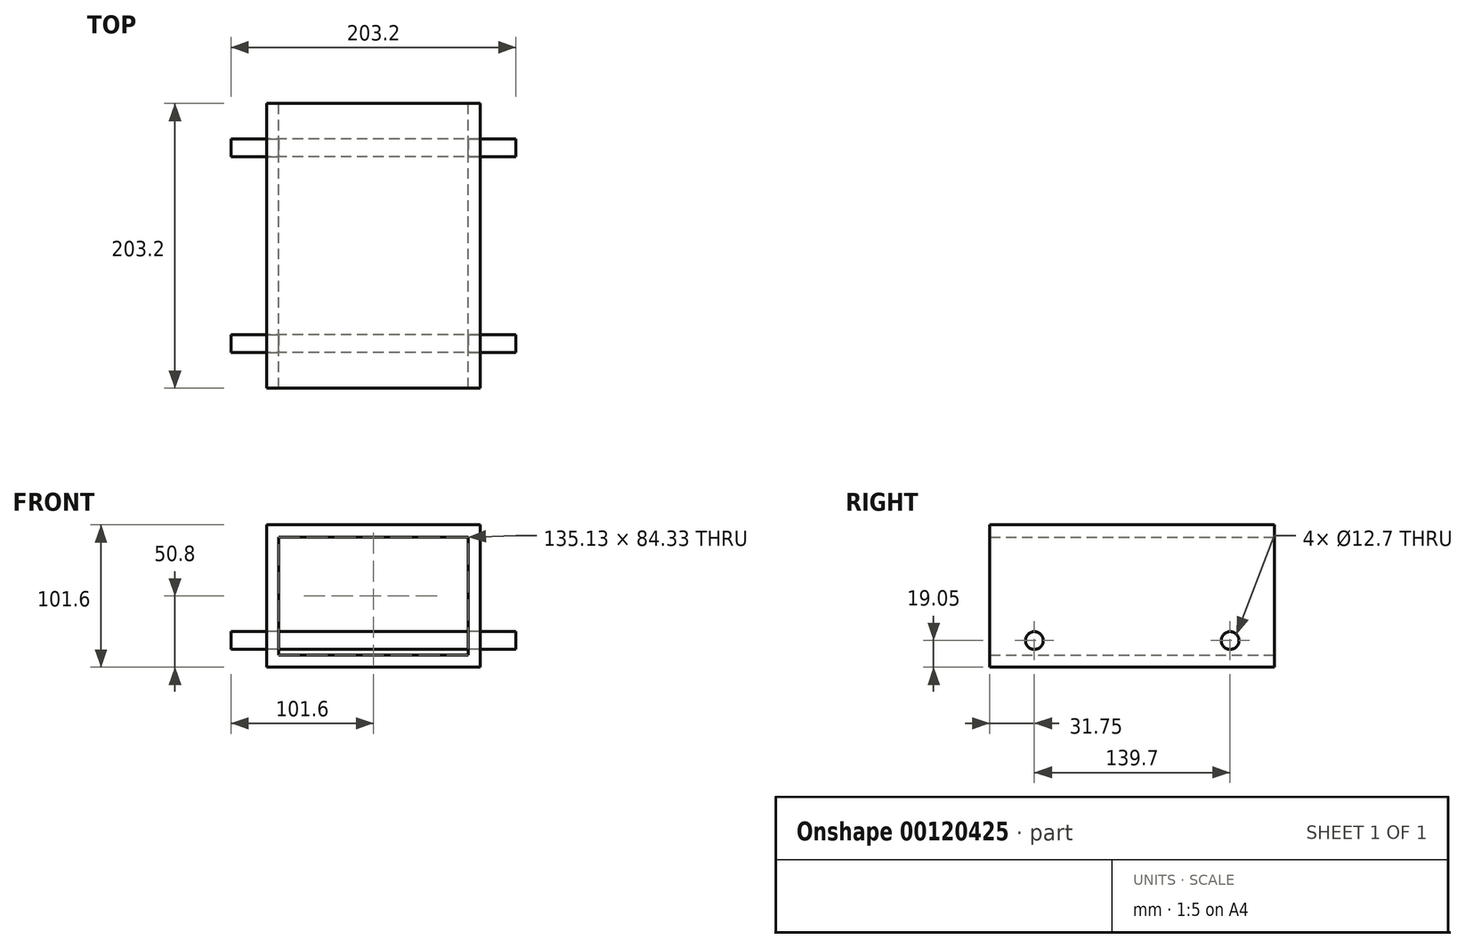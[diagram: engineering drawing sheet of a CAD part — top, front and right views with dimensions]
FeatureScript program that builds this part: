
annotation { "Feature Type Name" : "Feature", "Feature Type Description" : "" }
export const myFeature = defineFeature(function(context is Context, id is Id, definition is map)
    precondition{}
    {
        {
            var Q0;
            Q0=qCreatedBy(makeId("Front.planeOp"),FACE);
            var sketch = newSketch(context, id + "F0", { "sketchPlane" : qUnion([Q0])});
            skLineSegment(sketch, "E0.bottom", {"start": v(-76.2, 50.8) * mm, "end": v(76.2, 50.8) * mm});
            skLineSegment(sketch, "E0.top", {"start": v(-76.2, -50.8) * mm, "end": v(76.2, -50.8) * mm});
            skLineSegment(sketch, "E0.left", {"start": v(-76.2, 50.8) * mm, "end": v(-76.2, -50.8) * mm});
            skLineSegment(sketch, "E0.right", {"start": v(76.2, 50.8) * mm, "end": v(76.2, -50.8) * mm});
            skLineSegment(sketch, "E1.bottom", {"start": v(-67.56, 42.16) * mm, "end": v(67.56, 42.16) * mm});
            skLineSegment(sketch, "E1.top", {"start": v(-67.56, -42.16) * mm, "end": v(67.56, -42.16) * mm});
            skLineSegment(sketch, "E1.left", {"start": v(-67.56, 42.16) * mm, "end": v(-67.56, -42.16) * mm});
            skLineSegment(sketch, "E1.right", {"start": v(67.56, 42.16) * mm, "end": v(67.56, -42.16) * mm});
            skLineSegment(sketch, "E2", {"start": v(0, 42.16) * mm, "end": v(0, -42.16) * mm, "construction": true});
            skLineSegment(sketch, "E3", {"start": v(0, 42.16) * mm, "end": v(0, 50.8) * mm, "construction": true});
            skLineSegment(sketch, "E4", {"start": v(0, -42.16) * mm, "end": v(0, -50.8) * mm, "construction": true});
            skLineSegment(sketch, "E5", {"start": v(0, 0) * mm, "end": v(-67.56, 0) * mm, "construction": true});
            skLineSegment(sketch, "E6", {"start": v(0, 0) * mm, "end": v(67.56, 0) * mm, "construction": true});
            skLineSegment(sketch, "E7", {"start": v(-67.56, 0) * mm, "end": v(-76.2, 0) * mm, "construction": true});
            skLineSegment(sketch, "E8", {"start": v(67.56, 0) * mm, "end": v(76.2, 0) * mm, "construction": true});
            skSolve(sketch);
        }
        {
            var Q0;
            Q0=makeQuery(id+"F0.imprint","IMPRINT",FACE,{"disambiguationData":[TD([[makeQuery(id+"F0.imprint","IMPRINT",EDGE,{"derivedFrom":sQuery(id+"F0.wireOp",EDGE,"E0.bottom")}),-1.0]])]});
            extrude(context, id + "F1", {"entities" : qUnion([Q0]), "depth" : 203.2 * mm, "symmetric" : true});
        }
        {
            var Q0;
            Q0=makeQuery(id+"F1.opExtrude","SWEPT_FACE",FACE,{"disambiguationData":[OSD([sQuery(id+"F0.wireOp",EDGE,"E0.right")])]});
            var sketch = newSketch(context, id + "F2", { "sketchPlane" : qUnion([Q0])});
            skLineSegment(sketch, "E9", {"start": v(0, 0) * mm, "end": v(0, -31.75) * mm, "construction": true});
            skLineSegment(sketch, "E10", {"start": v(-69.85, -31.75) * mm, "end": v(69.85, -31.75) * mm, "construction": true});
            skCircle(sketch, "E11", {"center": v(-69.85, -31.75) * mm, "radius": 6.35 * mm});
            skCircle(sketch, "E12", {"center": v(69.85, -31.75) * mm, "radius": 6.35 * mm});
            skCircle(sketch, "E13", {"center": v(69.85, -31.75) * mm, "radius": 38.1 * mm, "construction": true});
            skCircle(sketch, "E14", {"center": v(-69.85, -31.75) * mm, "radius": 38.1 * mm, "construction": true});
            skSolve(sketch);
        }
        {
            var Q0;
            Q0=qSketchRegion(id+"F2",true);
            extrude(context, id + "F3", {"entities" : qUnion([Q0]), "operationType" : NewBodyOperationType.REMOVE, "endBound" : BoundingType.THROUGH_ALL, "oppositeDirection" : true, "depth" : 25.4 * mm});
        }
        {
            var Q0;
            Q0=qCreatedBy(makeId("Right.planeOp"),FACE);
            var sketch = newSketch(context, id + "F4", { "sketchPlane" : qUnion([Q0])});
            skCircle(sketch, "E15.0", {"center": v(-69.85, -31.75) * mm, "radius": 6.35 * mm});
            skCircle(sketch, "E16.0", {"center": v(69.85, -31.75) * mm, "radius": 6.35 * mm});
            skSolve(sketch);
        }
        {
            var Q0;
            Q0=makeQuery(id+"F4.imprint","IMPRINT",FACE,{"disambiguationData":[TD([[makeQuery(id+"F4.imprint","IMPRINT",EDGE,{"derivedFrom":sQuery(id+"F4.wireOp",EDGE,"E15.0")}),1.0]])]});
            var Q1;
            Q1=makeQuery(id+"F4.imprint","IMPRINT",FACE,{"disambiguationData":[TD([[makeQuery(id+"F4.imprint","IMPRINT",EDGE,{"derivedFrom":sQuery(id+"F4.wireOp",EDGE,"E16.0")}),1.0]])]});
            extrude(context, id + "F5", {"entities" : qUnion([Q0, Q1]), "depth" : 203.2 * mm, "symmetric" : true});
        }
    });
